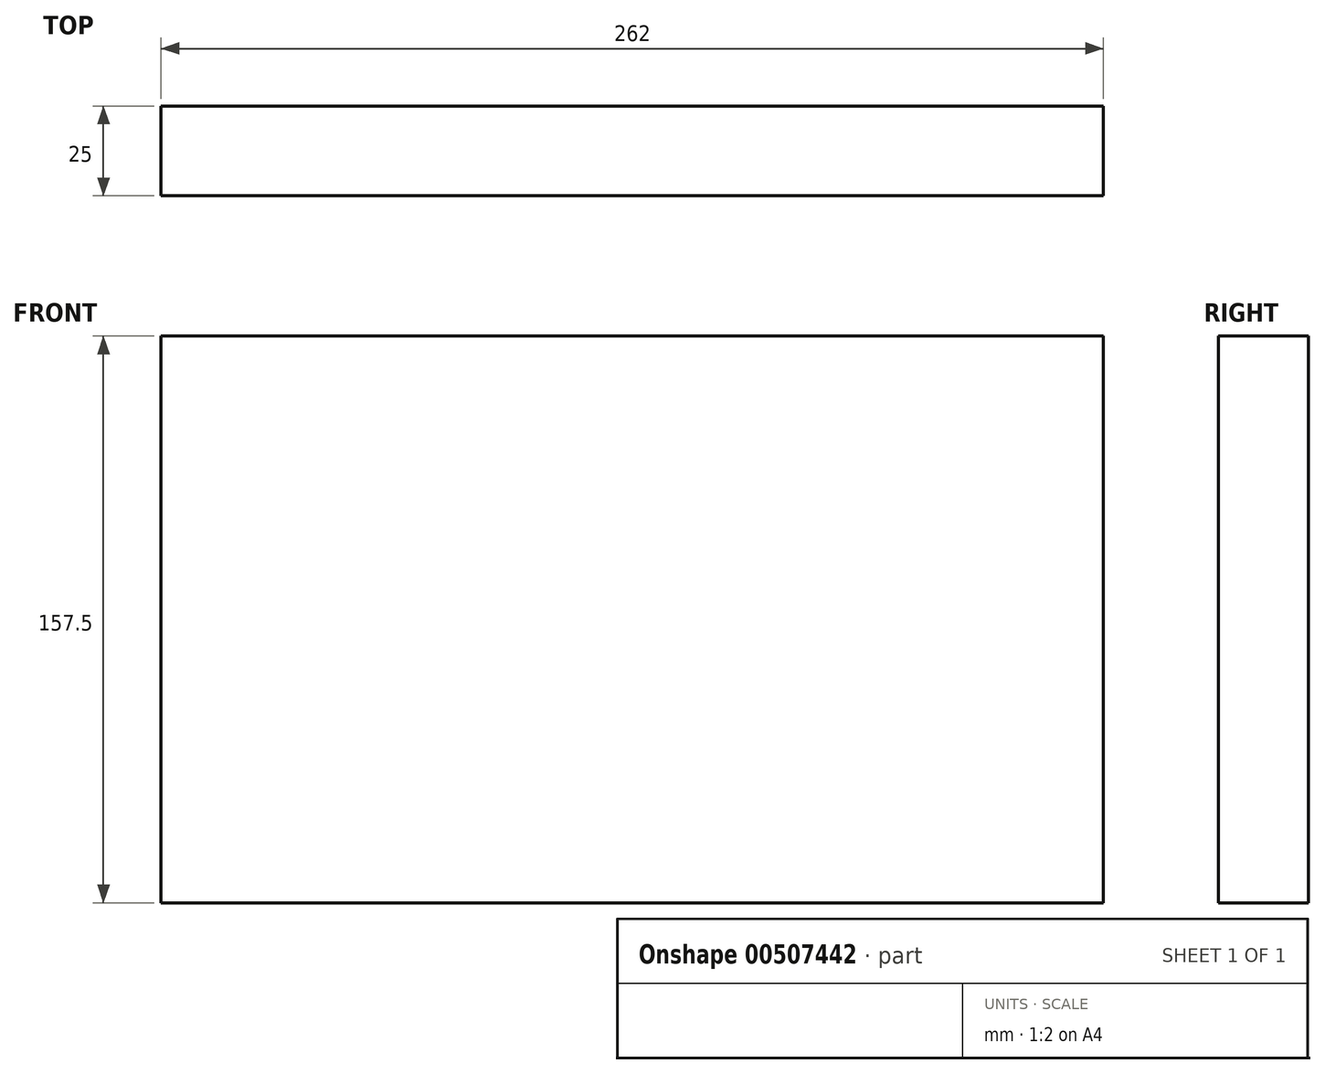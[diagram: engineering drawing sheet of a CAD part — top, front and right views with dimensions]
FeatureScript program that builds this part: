
annotation { "Feature Type Name" : "Feature", "Feature Type Description" : "" }
export const myFeature = defineFeature(function(context is Context, id is Id, definition is map)
    precondition{}
    {
        {
            var Q0;
            Q0=qCreatedBy(makeId("Front.planeOp"),FACE);
            var sketch = newSketch(context, id + "F0", { "sketchPlane" : qUnion([Q0])});
            skLineSegment(sketch, "E0.bottom", {"start": v(0, 0) * mm, "end": v(262, 0) * mm});
            skLineSegment(sketch, "E0.top", {"start": v(0, 157.5) * mm, "end": v(262, 157.5) * mm});
            skLineSegment(sketch, "E0.left", {"start": v(0, 0) * mm, "end": v(0, 157.5) * mm});
            skLineSegment(sketch, "E0.right", {"start": v(262, 0) * mm, "end": v(262, 157.5) * mm});
            skSolve(sketch);
        }
        {
            var Q0;
            Q0=makeQuery(id+"F0.imprint","IMPRINT",FACE,{"disambiguationData":[TD([[makeQuery(id+"F0.imprint","IMPRINT",EDGE,{"derivedFrom":sQuery(id+"F0.wireOp",EDGE,"E0.bottom")}),1.0]])]});
            extrude(context, id + "F1", {"entities" : qUnion([Q0]), "depth" : 25 * mm});
        }
    });
